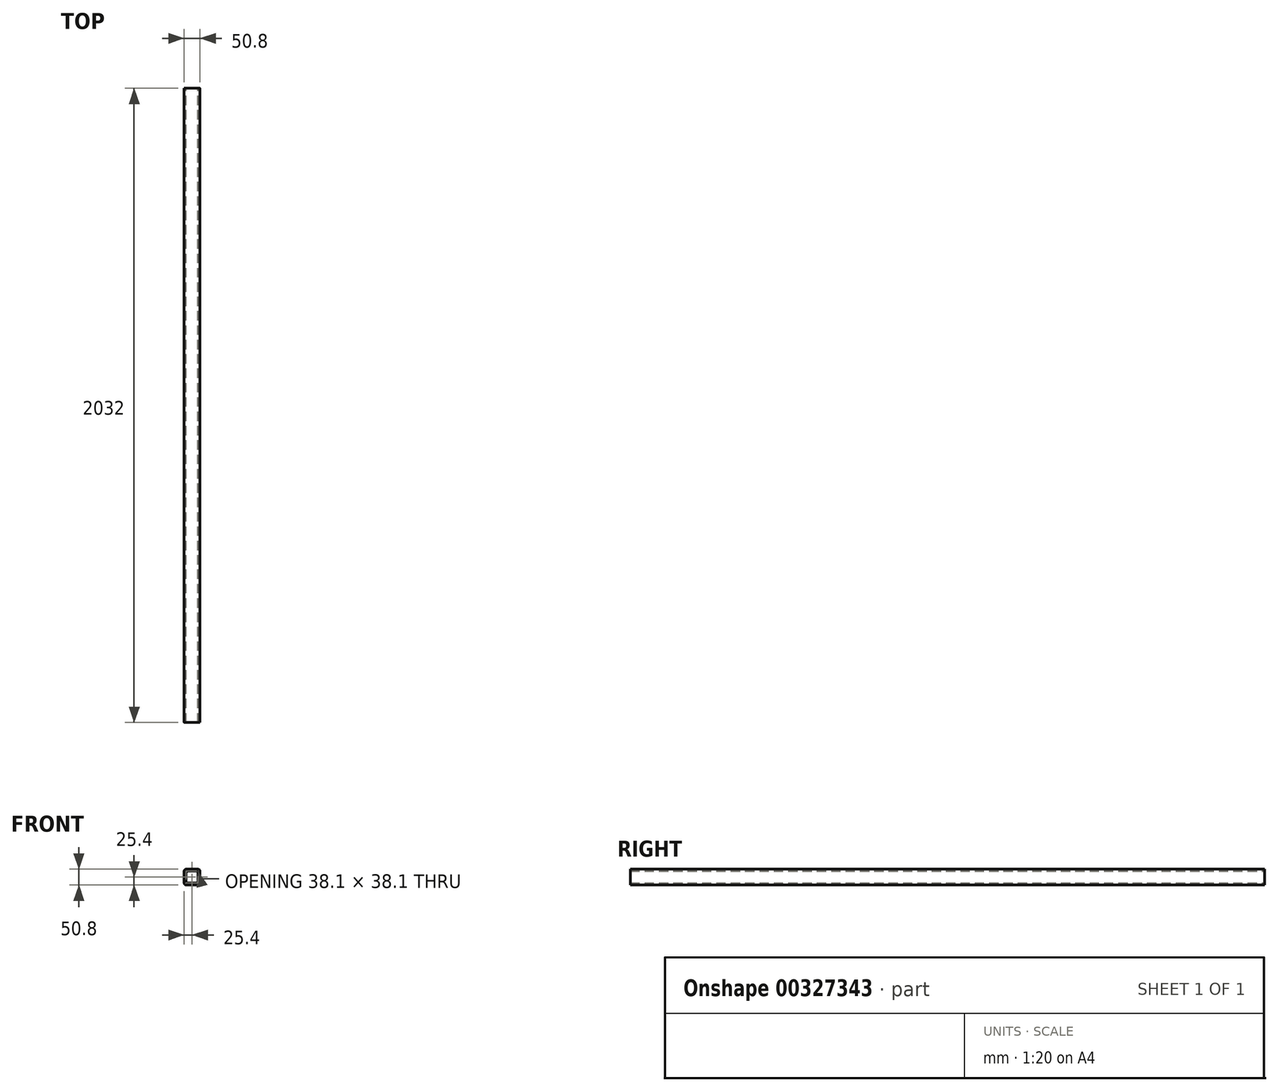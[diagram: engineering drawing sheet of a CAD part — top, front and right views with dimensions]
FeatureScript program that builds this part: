
annotation { "Feature Type Name" : "Feature", "Feature Type Description" : "" }
export const myFeature = defineFeature(function(context is Context, id is Id, definition is map)
    precondition{}
    {
        {
            var Q0;
            Q0=qCreatedBy(makeId("Front.planeOp"),FACE);
            var sketch = newSketch(context, id + "F0", { "sketchPlane" : qUnion([Q0])});
            skLineSegment(sketch, "E0.bottom", {"start": v(-25.4, 25.4) * mm, "end": v(25.4, 25.4) * mm});
            skLineSegment(sketch, "E0.top", {"start": v(-25.4, -25.4) * mm, "end": v(25.4, -25.4) * mm});
            skLineSegment(sketch, "E0.left", {"start": v(-25.4, 25.4) * mm, "end": v(-25.4, -25.4) * mm});
            skLineSegment(sketch, "E0.right", {"start": v(25.4, 25.4) * mm, "end": v(25.4, -25.4) * mm});
            skLineSegment(sketch, "E1.bottom", {"start": v(-19.05, 19.05) * mm, "end": v(19.05, 19.05) * mm});
            skLineSegment(sketch, "E1.top", {"start": v(-19.05, -19.05) * mm, "end": v(19.05, -19.05) * mm});
            skLineSegment(sketch, "E1.left", {"start": v(-19.05, 19.05) * mm, "end": v(-19.05, -19.05) * mm});
            skLineSegment(sketch, "E1.right", {"start": v(19.05, 19.05) * mm, "end": v(19.05, -19.05) * mm});
            skSolve(sketch);
        }
        {
            var Q0;
            Q0=makeQuery(id+"F0.imprint","IMPRINT",FACE,{"disambiguationData":[TD([[makeQuery(id+"F0.imprint","IMPRINT",EDGE,{"derivedFrom":sQuery(id+"F0.wireOp",EDGE,"E0.bottom")}),-1.0]])]});
            extrude(context, id + "F1", {"entities" : qUnion([Q0]), "depth" : 2032 * mm});
        }
        {
            var Q0;
            Q0=makeQuery(id+"F1.opExtrude","SWEPT_EDGE",EDGE,{"disambiguationData":[OSD([sQuery(id+"F0.wireOp",EDGE,"E0.bottom"),sQuery(id+"F0.wireOp",EDGE,"E0.right")])]});
            var Q1;
            Q1=makeQuery(id+"F1.opExtrude","SWEPT_EDGE",EDGE,{"disambiguationData":[OSD([sQuery(id+"F0.wireOp",EDGE,"E0.top"),sQuery(id+"F0.wireOp",EDGE,"E0.right")])]});
            var Q2;
            Q2=makeQuery(id+"F1.opExtrude","SWEPT_EDGE",EDGE,{"disambiguationData":[OSD([sQuery(id+"F0.wireOp",EDGE,"E0.bottom"),sQuery(id+"F0.wireOp",EDGE,"E0.left")])]});
            var Q3;
            Q3=makeQuery(id+"F1.opExtrude","SWEPT_EDGE",EDGE,{"disambiguationData":[OSD([sQuery(id+"F0.wireOp",EDGE,"E0.top"),sQuery(id+"F0.wireOp",EDGE,"E0.left")])]});
            var Q4;
            Q4=makeQuery(id+"F1.opExtrude","SWEPT_EDGE",EDGE,{"disambiguationData":[OSD([sQuery(id+"F0.wireOp",EDGE,"E1.top"),sQuery(id+"F0.wireOp",EDGE,"E1.left")])]});
            var Q5;
            Q5=makeQuery(id+"F1.opExtrude","SWEPT_EDGE",EDGE,{"disambiguationData":[OSD([sQuery(id+"F0.wireOp",EDGE,"E1.top"),sQuery(id+"F0.wireOp",EDGE,"E1.right")])]});
            var Q6;
            Q6=makeQuery(id+"F1.opExtrude","SWEPT_EDGE",EDGE,{"disambiguationData":[OSD([sQuery(id+"F0.wireOp",EDGE,"E1.bottom"),sQuery(id+"F0.wireOp",EDGE,"E1.right")])]});
            var Q7;
            Q7=makeQuery(id+"F1.opExtrude","SWEPT_EDGE",EDGE,{"disambiguationData":[OSD([sQuery(id+"F0.wireOp",EDGE,"E1.bottom"),sQuery(id+"F0.wireOp",EDGE,"E1.left")])]});
            fillet(context, id + "F2", {"entities" : qUnion([Q0, Q1, Q2, Q3, Q4, Q5, Q6, Q7]), "radius" : 6.35 * mm, "tangentPropagation" : true, "allowEdgeOverflow" : false});
        }
    });
